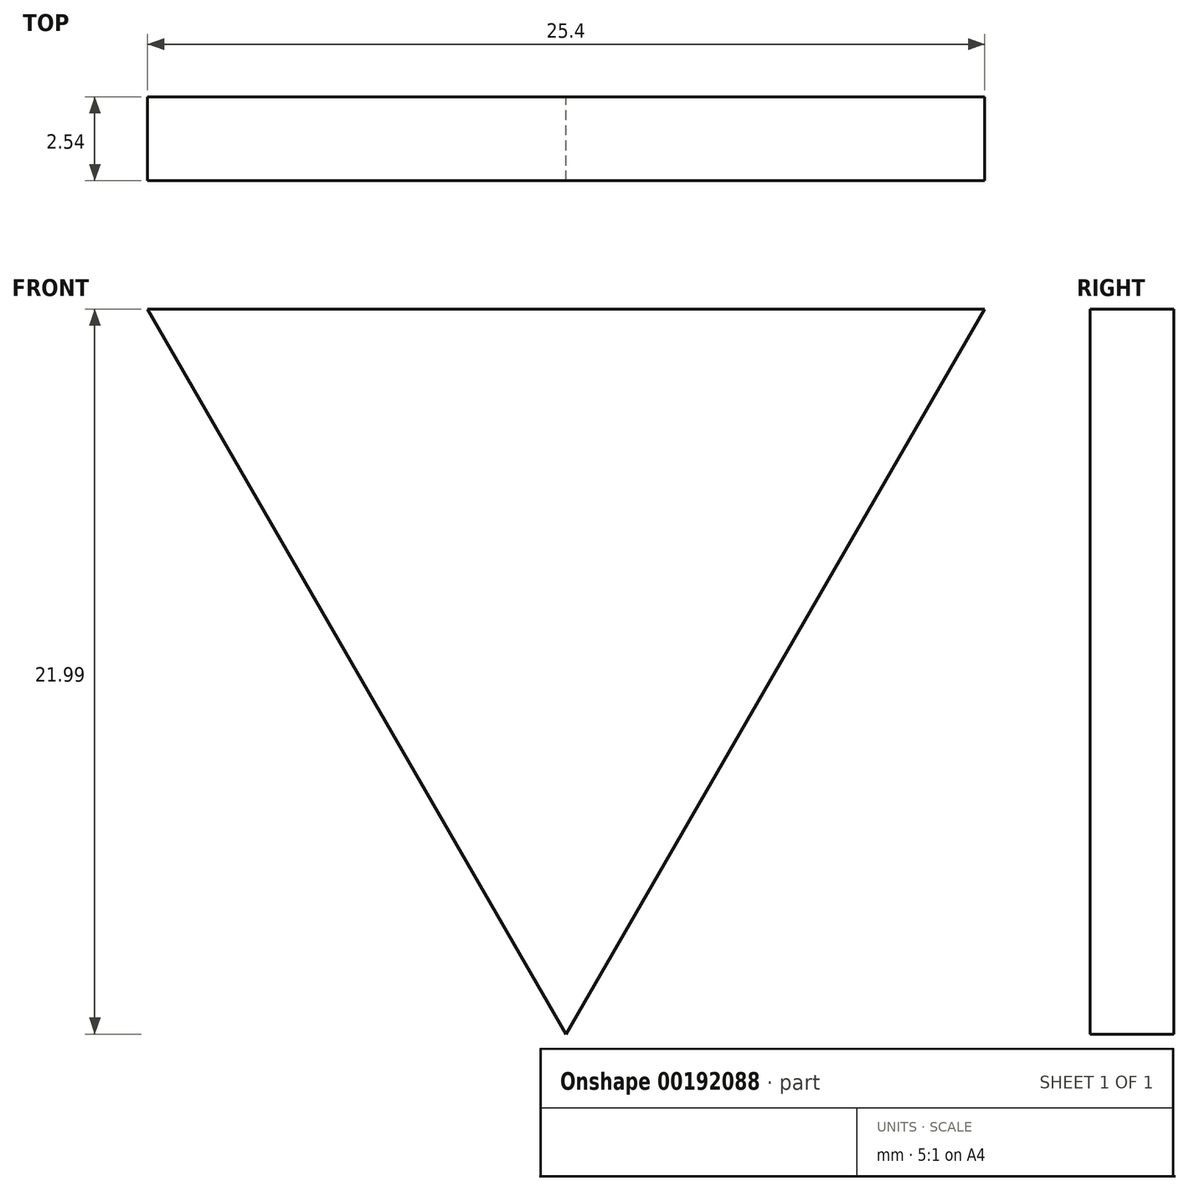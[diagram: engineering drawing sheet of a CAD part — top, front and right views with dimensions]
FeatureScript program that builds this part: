
annotation { "Feature Type Name" : "Feature", "Feature Type Description" : "" }
export const myFeature = defineFeature(function(context is Context, id is Id, definition is map)
    precondition{}
    {
        {
            var Q0;
            Q0=qCreatedBy(makeId("Front.planeOp"),FACE);
            var sketch = newSketch(context, id + "F0", { "sketchPlane" : qUnion([Q0])});
            skCircle(sketch, "E0.cCircle", {"center": v(0, 0) * mm, "radius": 7.33 * mm, "construction": true});
            skLineSegment(sketch, "E0.0", {"start": v(-12.7, 7.33) * mm, "end": v(12.7, 7.33) * mm});
            skLineSegment(sketch, "E0.1", {"start": v(12.7, 7.33) * mm, "end": v(0, -14.66) * mm});
            skLineSegment(sketch, "E0.2", {"start": v(0, -14.66) * mm, "end": v(-12.7, 7.33) * mm});
            skPoint(sketch, "E0.0.midPoint", {"position": v(0, 7.33) * mm});
            skLineSegment(sketch, "E1", {"start": v(0, 7.33) * mm, "end": v(-6.35, -3.67) * mm});
            skLineSegment(sketch, "E2", {"start": v(-6.35, -3.67) * mm, "end": v(6.35, -3.67) * mm});
            skLineSegment(sketch, "E3", {"start": v(6.35, -3.67) * mm, "end": v(0, 7.33) * mm});
            skSolve(sketch);
        }
        {
            var Q0;
            {var subQ3=sQuery(id+"F0.wireOp",EDGE,"E3");Q0=makeQuery(id+"F0.imprint","IMPRINT",FACE,{"disambiguationData":[TD([[makeQuery(id+"F0.imprint","IMPRINT",EDGE,{"derivedFrom":subQ3}),-1.0]])]});}
            var Q1;
            {var subQ3=sQuery(id+"F0.wireOp",EDGE,"E2");Q1=makeQuery(id+"F0.imprint","IMPRINT",FACE,{"disambiguationData":[TD([[makeQuery(id+"F0.imprint","IMPRINT",EDGE,{"derivedFrom":subQ3}),-1.0]])]});}
            var Q2;
            {var subQ3=sQuery(id+"F0.wireOp",EDGE,"E1");Q2=makeQuery(id+"F0.imprint","IMPRINT",FACE,{"disambiguationData":[TD([[makeQuery(id+"F0.imprint","IMPRINT",EDGE,{"derivedFrom":subQ3}),-1.0]])]});}
            var Q3;
            Q3=makeQuery(id+"F0.imprint","IMPRINT",FACE,{"disambiguationData":[TD([[makeQuery(id+"F0.imprint","IMPRINT",EDGE,{"derivedFrom":sQuery(id+"F0.wireOp",EDGE,"E1")}),1.0]])]});
            extrude(context, id + "F1", {"entities" : qUnion([Q0, Q1, Q2, Q3]), "depth" : 2.54 * mm});
        }
    });
